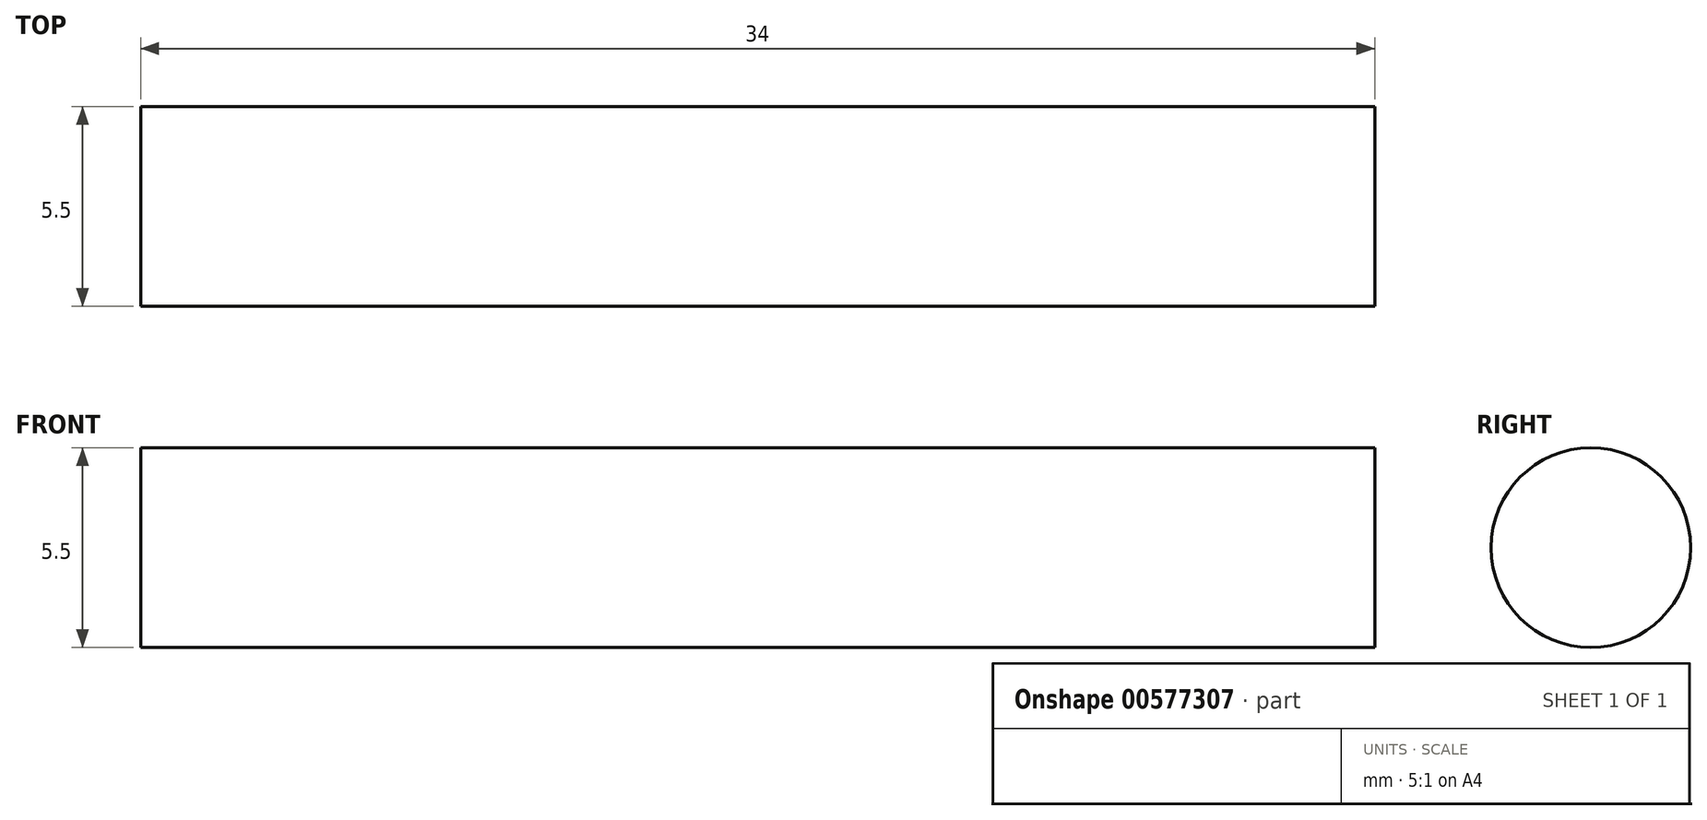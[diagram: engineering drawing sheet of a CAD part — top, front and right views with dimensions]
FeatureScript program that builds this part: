
annotation { "Feature Type Name" : "Feature", "Feature Type Description" : "" }
export const myFeature = defineFeature(function(context is Context, id is Id, definition is map)
    precondition{}
    {
        {
            var Q0;
            Q0=qCreatedBy(makeId("Right.planeOp"),FACE);
            var sketch = newSketch(context, id + "F0", { "sketchPlane" : qUnion([Q0])});
            skCircle(sketch, "E0", {"center": v(0, 0) * mm, "radius": 2.75 * mm});
            skSolve(sketch);
        }
        {
            var Q0;
            Q0 = qSketchRegion(id + "F0", true);
            extrude(context, id + "F1", {"entities" : qUnion([Q0]), "depth" : 34 * mm, "offsetDistance" : 25 * mm});
        }
    });
